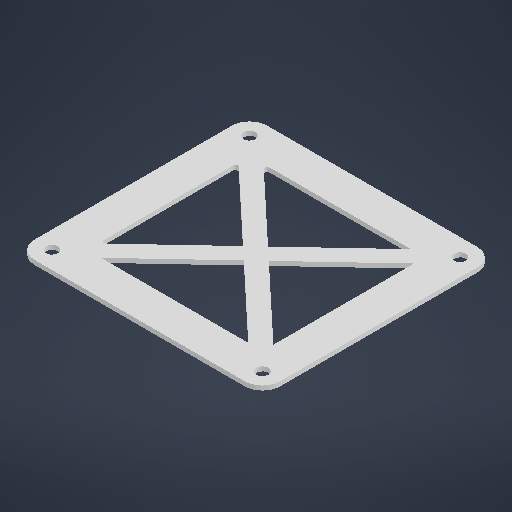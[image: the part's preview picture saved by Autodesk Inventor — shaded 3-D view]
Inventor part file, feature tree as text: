
AUTODESK INVENTOR PART (.ipt)
format: ipt  version: 2025.2 (Build 292293000, 293)  size: 233,472 bytes
history: native  units: in
note: dims shown in document units (in); Inventor stores cm internally (conversion verified against a paired STEP export)
features: extrude x1, sketch x1
ambient origin geometry x8: Origin, YZ Plane, XZ Plane, XY Plane, X Axis, Y Axis, Z Axis, Center Point
bodies: Solid1 (feature_tree)
feature tree (2):
  extrude  "Extrusion1"  Depth=0.5in
  sketch  "Sketch1"  dims[d0=0.5in d1=0.5in d2=0.5in d3=0.5in d8=0.25in d11=0.25in d14=0.25in d16=0.25in d17=0.25in d18=0.25in d19=0.25in d20=0.25in d21=0.035in d22=0.035in d23=0.035in d24=0.035in d25=0.035in d26=0.035in d27=0.035in d28=0.035in d29=0.0625in d30=0.0in]
